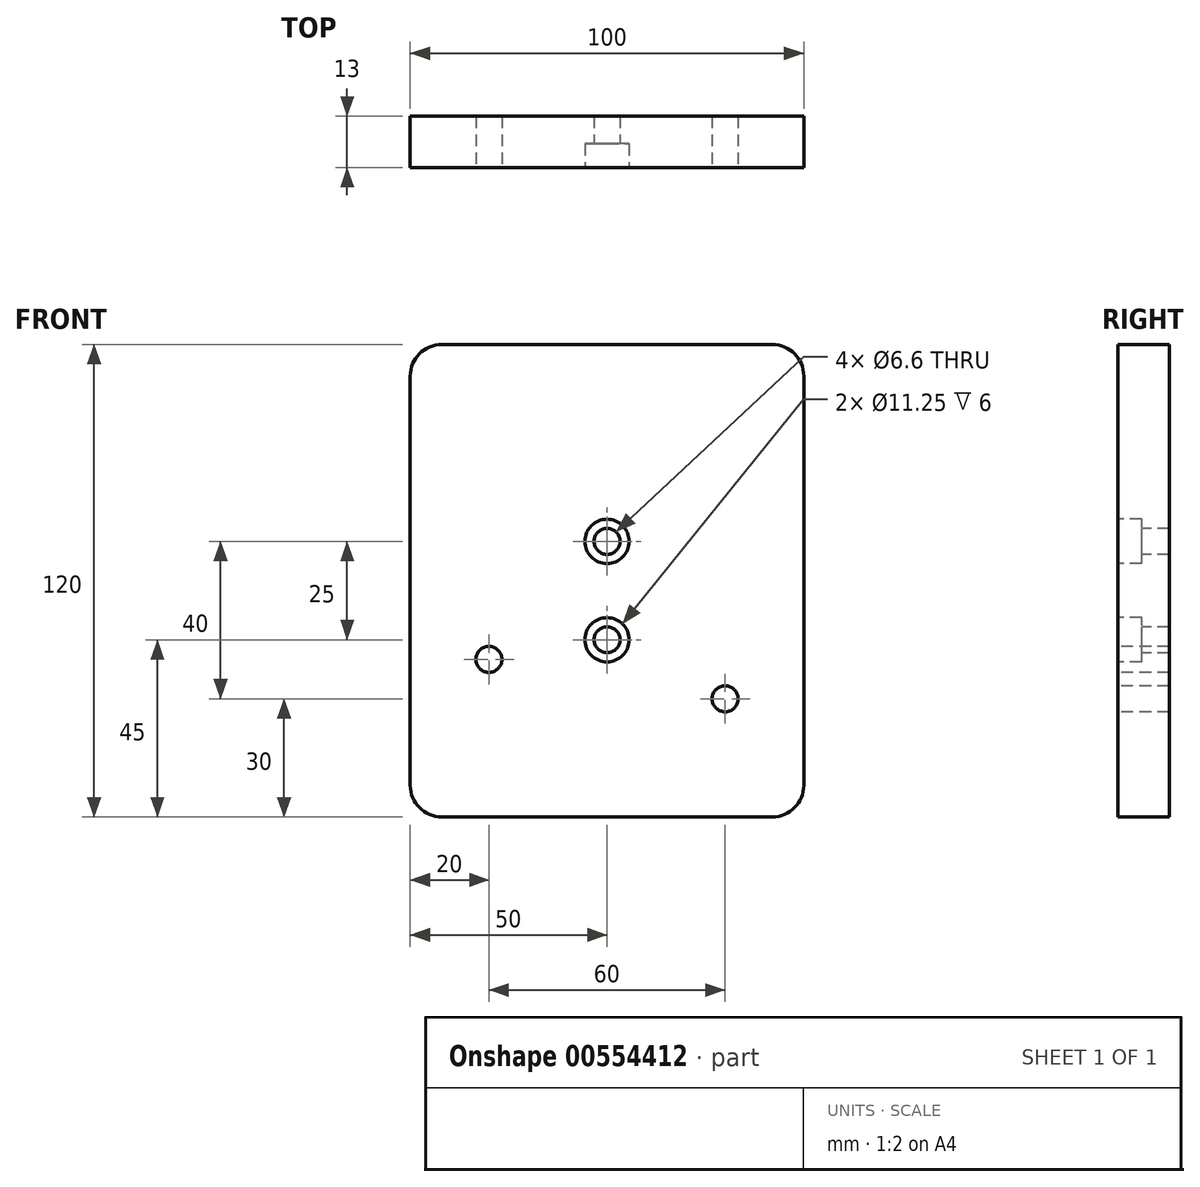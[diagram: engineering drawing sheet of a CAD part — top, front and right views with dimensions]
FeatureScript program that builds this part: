
annotation { "Feature Type Name" : "Feature", "Feature Type Description" : "" }
export const myFeature = defineFeature(function(context is Context, id is Id, definition is map)
    precondition{}
    {
        {
            var Q0;
            Q0=qCreatedBy(makeId("Front.planeOp"),FACE);
            var sketch = newSketch(context, id + "F0", { "sketchPlane" : qUnion([Q0])});
            skLineSegment(sketch, "E0.bottom", {"start": v(0, 0) * mm, "end": v(100, 0) * mm});
            skLineSegment(sketch, "E0.top", {"start": v(0, 120) * mm, "end": v(100, 120) * mm});
            skLineSegment(sketch, "E0.left", {"start": v(0, 0) * mm, "end": v(0, 120) * mm});
            skLineSegment(sketch, "E0.right", {"start": v(100, 0) * mm, "end": v(100, 120) * mm});
            skSolve(sketch);
        }
        {
            var Q0;
            Q0 = qSketchRegion(id + "F0", true);
            var Q1;
            Q1=makeQuery(id+"F0.imprint","IMPRINT",FACE,{"disambiguationData":[TD([[makeQuery(id+"F0.imprint","IMPRINT",EDGE,{"derivedFrom":sQuery(id+"F0.wireOp",EDGE,"E0.bottom")}),1.0]])]});
            extrude(context, id + "F1", {"entities" : qUnion([Q0, Q1]), "depth" : 13 * mm, "offsetDistance" : 25 * mm});
        }
        {
            var Q0;
            Q0=makeQuery(id+"F1.opExtrude","CAP_FACE",FACE,{"disambiguationData":[OSD([sQuery(id+"F0.wireOp",EDGE,"E0.bottom"),sQuery(id+"F0.wireOp",EDGE,"E0.top"),sQuery(id+"F0.wireOp",EDGE,"E0.left"),sQuery(id+"F0.wireOp",EDGE,"E0.right")])],"isStart":false});
            var sketch = newSketch(context, id + "F2", { "sketchPlane" : qUnion([Q0])});
            skPoint(sketch, "E1", {"position": v(80, 30) * mm});
            skPoint(sketch, "E2", {"position": v(20, 40) * mm});
            skPoint(sketch, "E3", {"position": v(50, 70) * mm});
            skPoint(sketch, "E3.positionSnap0", {"position": v(50, 120) * mm});
            skPoint(sketch, "E4", {"position": v(50, 45) * mm});
            skSolve(sketch);
        }
        {
            var Q0;
            Q0=sQuery(id+"F2.wireOp",VERTEX,"E1");
            var Q1;
            Q1=sQuery(id+"F2.wireOp",VERTEX,"E2");
            var Q2;
            Q2=makeQuery(id+"F1.opExtrude","SWEPT_BODY",BODY,{"disambiguationData":[OSD([sQuery(id+"F0.wireOp",EDGE,"E0.bottom"),sQuery(id+"F0.wireOp",EDGE,"E0.top"),sQuery(id+"F0.wireOp",EDGE,"E0.left"),sQuery(id+"F0.wireOp",EDGE,"E0.right")])]});
            hole(context, id + "F3", {"style" : HoleStyle.SIMPLE, "endStyle" : HoleEndStyle.THROUGH, "standardTappedOrClearance" : lookupTablePath({ "standard" : "ISO", "fit" : "Normal", "size" : "M6", "type" : "Clearance" }), "standardBlindInLast" : lookupTablePath({ "fit" : "Standard", "standard" : "ISO", "size" : "M6", "type" : "Clearance" }), "holeDiameter" : 6.6 * mm, "isTappedThrough" : true, "tappedDepth" : 8 * mm, "tapClearance" : 3, "startFromSketch" : true, "locations" : qUnion([Q0, Q1]), "scope" : qUnion([Q2])});
        }
        {
            var Q0;
            Q0=sQuery(id+"F2.wireOp",VERTEX,"E3");
            var Q1;
            Q1=sQuery(id+"F2.wireOp",VERTEX,"E4");
            var Q2;
            Q2=makeQuery(id+"F1.opExtrude","SWEPT_BODY",BODY,{"disambiguationData":[OSD([sQuery(id+"F0.wireOp",EDGE,"E0.bottom"),sQuery(id+"F0.wireOp",EDGE,"E0.top"),sQuery(id+"F0.wireOp",EDGE,"E0.left"),sQuery(id+"F0.wireOp",EDGE,"E0.right")])]});
            hole(context, id + "F4", {"style" : HoleStyle.C_BORE, "endStyle" : HoleEndStyle.THROUGH, "standardTappedOrClearance" : lookupTablePath({ "standard" : "ISO", "fit" : "Normal", "size" : "M6", "type" : "Clearance" }), "standardBlindInLast" : lookupTablePath({ "fit" : "Standard", "standard" : "ISO", "size" : "M6", "type" : "Clearance" }), "holeDiameter" : 6.6 * mm, "cBoreDiameter" : 11.25 * mm, "cBoreDepth" : 6 * mm, "isTappedThrough" : true, "tappedDepth" : 8 * mm, "tapClearance" : 3, "startFromSketch" : true, "locations" : qUnion([Q0, Q1]), "scope" : qUnion([Q2])});
        }
        {
            var Q0;
            Q0=makeQuery(id+"F1.opExtrude","SWEPT_EDGE",EDGE,{"disambiguationData":[OSD([sQuery(id+"F0.wireOp",EDGE,"E0.top"),sQuery(id+"F0.wireOp",EDGE,"E0.right")])]});
            var Q1;
            Q1=makeQuery(id+"F1.opExtrude","SWEPT_EDGE",EDGE,{"disambiguationData":[OSD([sQuery(id+"F0.wireOp",EDGE,"E0.bottom"),sQuery(id+"F0.wireOp",EDGE,"E0.right")])]});
            var Q2;
            Q2=makeQuery(id+"F1.opExtrude","SWEPT_EDGE",EDGE,{"disambiguationData":[OSD([sQuery(id+"F0.wireOp",EDGE,"E0.top"),sQuery(id+"F0.wireOp",EDGE,"E0.left")])]});
            var Q3;
            Q3=makeQuery(id+"F1.opExtrude","SWEPT_EDGE",EDGE,{"disambiguationData":[OSD([sQuery(id+"F0.wireOp",EDGE,"E0.bottom"),sQuery(id+"F0.wireOp",EDGE,"E0.left")])]});
            fillet(context, id + "F5", {"entities" : qUnion([Q0, Q1, Q2, Q3]), "radius" : 8 * mm, "tangentPropagation" : true, "allowEdgeOverflow" : false});
        }
    });
